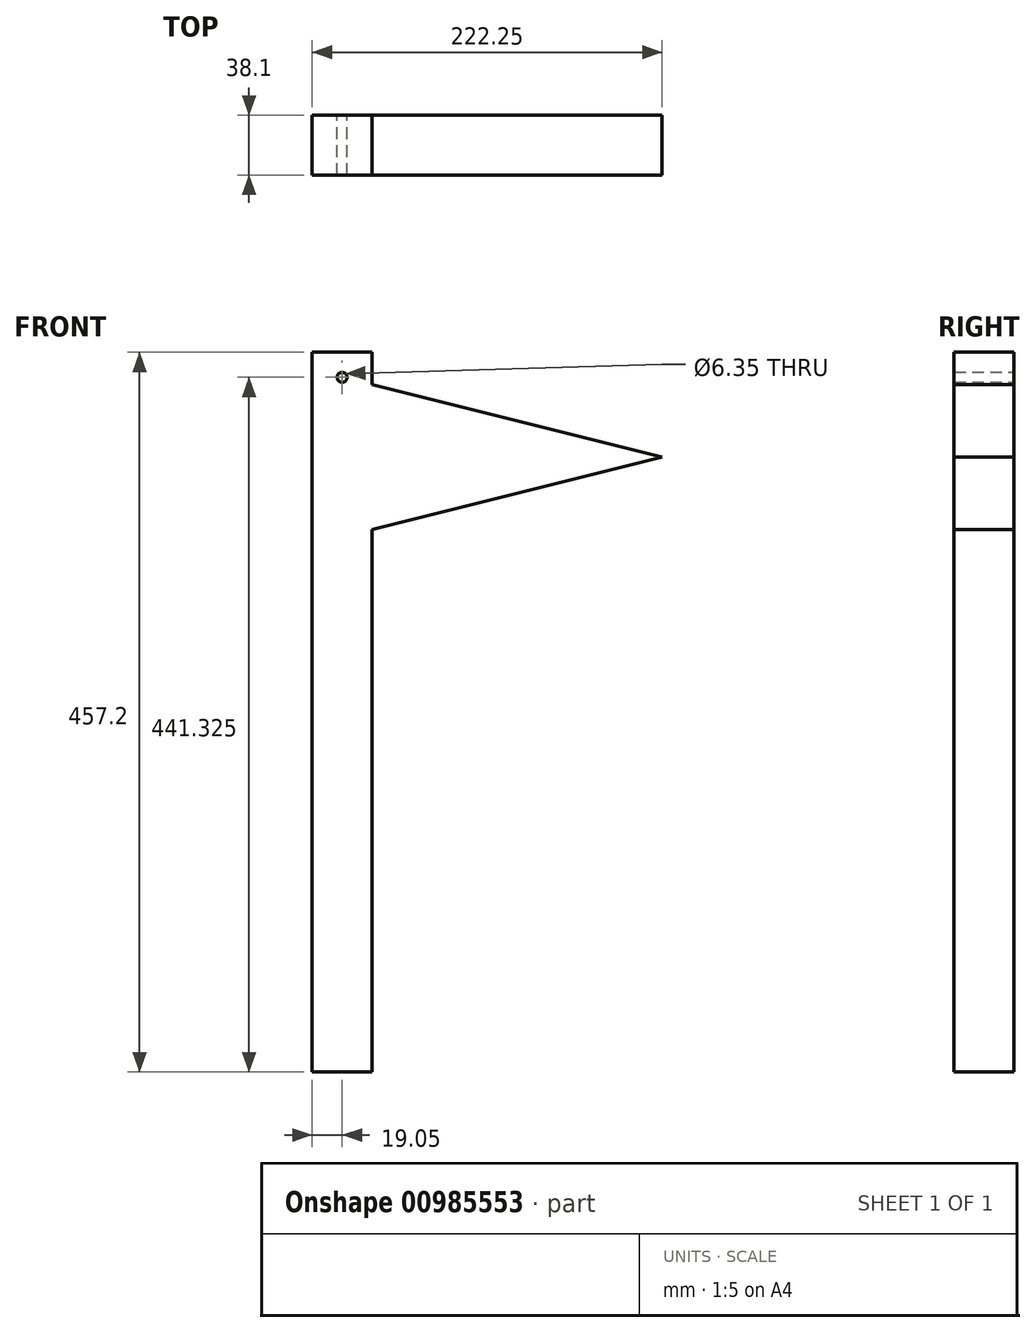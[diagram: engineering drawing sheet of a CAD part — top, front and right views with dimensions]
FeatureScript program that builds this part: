
annotation { "Feature Type Name" : "Feature", "Feature Type Description" : "" }
export const myFeature = defineFeature(function(context is Context, id is Id, definition is map)
    precondition{}
    {
        {
            var Q0;
            Q0=qCreatedBy(makeId("Front.planeOp"),FACE);
            var sketch = newSketch(context, id + "F0", { "sketchPlane" : qUnion([Q0])});
            skLineSegment(sketch, "E0", {"start": v(0, 0) * mm, "end": v(0, 457.2) * mm});
            skLineSegment(sketch, "E1", {"start": v(0, 457.2) * mm, "end": v(38.1, 457.2) * mm});
            skLineSegment(sketch, "E2", {"start": v(38.1, 457.2) * mm, "end": v(38.1, 0) * mm});
            skLineSegment(sketch, "E3", {"start": v(38.1, 0) * mm, "end": v(0, 0) * mm});
            skCircle(sketch, "E4", {"center": v(19.05, 441.33) * mm, "radius": 3.18 * mm});
            skPoint(sketch, "E4.centerSnap0", {"position": v(19.05, 457.2) * mm});
            skLineSegment(sketch, "E5", {"start": v(19.05, 441.33) * mm, "end": v(425.45, 339.73) * mm});
            skLineSegment(sketch, "E6", {"start": v(19.05, 441.33) * mm, "end": v(425.45, 441.33) * mm, "construction": true});
            skLineSegment(sketch, "E7", {"start": v(425.45, 339.73) * mm, "end": v(19.05, 339.72) * mm, "construction": true});
            skLineSegment(sketch, "E8", {"start": v(19.05, 339.72) * mm, "end": v(425.45, 441.33) * mm});
            skSolve(sketch);
        }
        {
            var Q0;
            Q0 = qSketchRegion(id + "F0", true);
            extrude(context, id + "F1", {"entities" : qUnion([Q0]), "depth" : 38.1 * mm, "offsetDistance" : 25.4 * mm});
        }
    });
